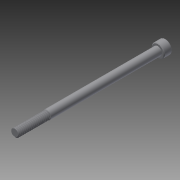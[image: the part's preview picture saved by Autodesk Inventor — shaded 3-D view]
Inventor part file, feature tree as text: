
AUTODESK INVENTOR PART (.ipt)
format: ipt  version: 2014 SP1 (Build 180222100, 222)  size: 479,744 bytes
history: native  units: in
note: dims shown in document units (in); Inventor stores cm internally (conversion verified against a paired STEP export)
features: other x2, extrude x1, imported_body x1, sketch x1
ambient origin geometry x8: Origin, YZ Plane, XZ Plane, XY Plane, X Axis, Y Axis, Z Axis, Center Point
bodies: Body1 (feature_tree)
feature tree (5):
  parser-record x1  (decoder bookkeeping rows leaked as tree rows — omitted from the tree; the rows remain in map.json)
  other  "91251A0851"
  extrude  "Extrusion1"  Depth=0.125in TaperAngle=0.0deg
  imported_body  "Base1"
  sketch  "Sketch1"  dims[d0=0.5in d1=0.125in d2=0.0in]
